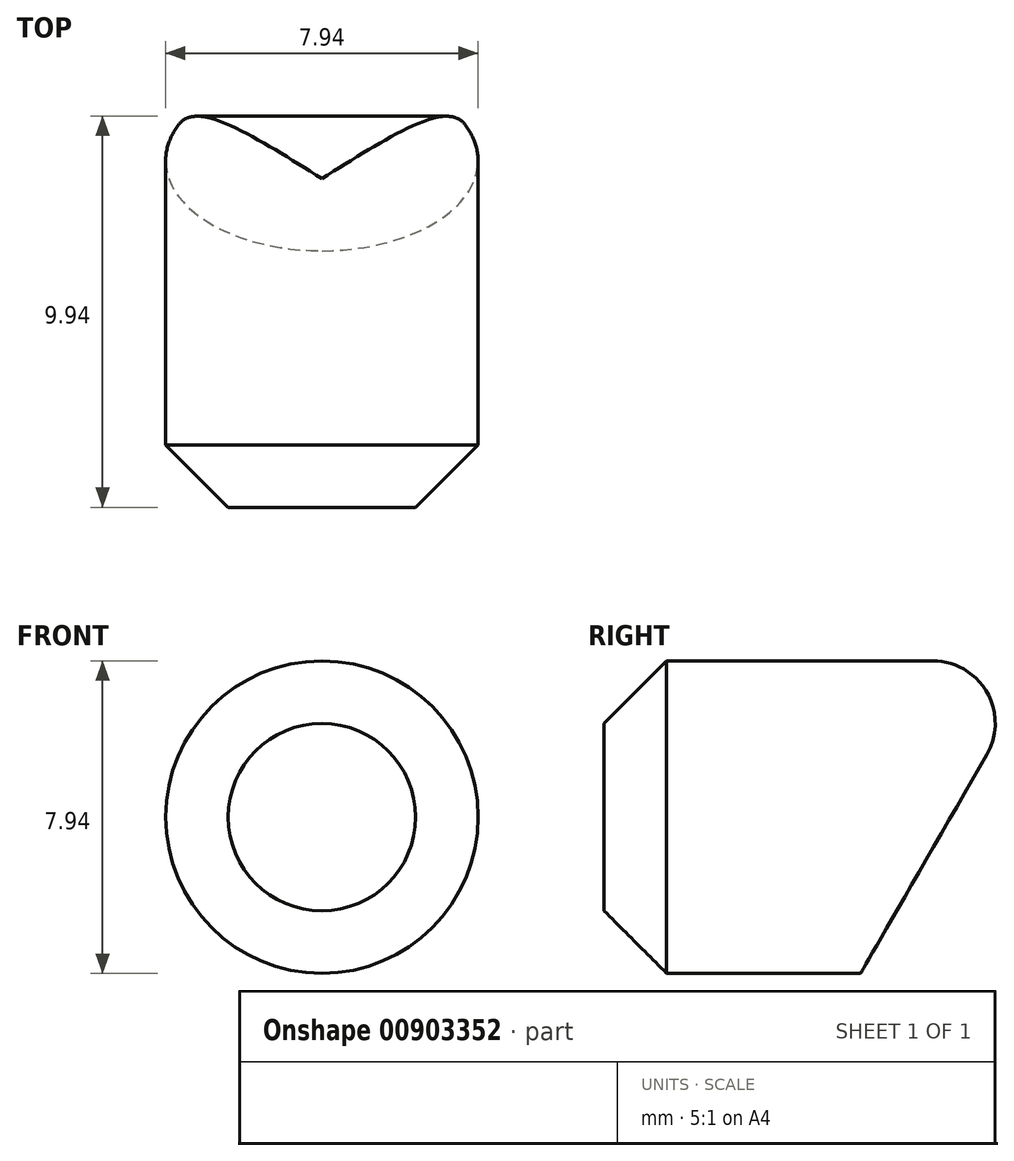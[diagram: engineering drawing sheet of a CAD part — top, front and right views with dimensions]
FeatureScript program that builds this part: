
annotation { "Feature Type Name" : "Feature", "Feature Type Description" : "" }
export const myFeature = defineFeature(function(context is Context, id is Id, definition is map)
    precondition{}
    {
        {
            var Q0;
            Q0=qCreatedBy(makeId("Front.planeOp"),FACE);
            var sketch = newSketch(context, id + "F0", { "sketchPlane" : qUnion([Q0])});
            skCircle(sketch, "E0", {"center": v(0, 0) * mm, "radius": 3.97 * mm});
            skSolve(sketch);
        }
        {
            var Q0;
            Q0=makeQuery(id+"F0.imprint","IMPRINT",FACE,{"disambiguationData":[TD([[makeQuery(id+"F0.imprint","IMPRINT",EDGE,{"derivedFrom":sQuery(id+"F0.wireOp",EDGE,"E0")}),1.0]])]});
            extrude(context, id + "F1", {"entities" : qUnion([Q0]), "oppositeDirection" : true, "depth" : 11.1 * mm, "offsetDistance" : 25.4 * mm});
        }
        {
            var Q0;
            Q0=qCreatedBy(makeId("Right.planeOp"),FACE);
            var sketch = newSketch(context, id + "F2", { "sketchPlane" : qUnion([Q0])});
            skLineSegment(sketch, "E1", {"start": v(11.1, 3.97) * mm, "end": v(-3.56, -21.43) * mm});
            skLineSegment(sketch, "E2", {"start": v(-3.56, -21.43) * mm, "end": v(11.1, -21.43) * mm});
            skLineSegment(sketch, "E3", {"start": v(11.1, -21.43) * mm, "end": v(11.1, 3.97) * mm});
            skLineSegment(sketch, "E4", {"start": v(0, 3.97) * mm, "end": v(11.1, 3.97) * mm});
            skSolve(sketch);
        }
        {
            var Q0;
            Q0=makeQuery(id+"F2.imprint","IMPRINT",FACE,{"disambiguationData":[TD([[makeQuery(id+"F2.imprint","IMPRINT",EDGE,{"derivedFrom":sQuery(id+"F2.wireOp",EDGE,"E1")}),1.0]])]});
            extrude(context, id + "F3", {"entities" : qUnion([Q0]), "operationType" : NewBodyOperationType.REMOVE, "oppositeDirection" : true, "depth" : 25.4 * mm, "offsetDistance" : 25.4 * mm, "hasSecondDirection" : true, "secondDirectionOppositeDirection" : false, "secondDirectionDepth" : 25.4 * mm});
        }
        {
            var Q0;
            Q0=makeQuery(id+"F1.opExtrude","CAP_EDGE",EDGE,{"disambiguationData":[OSD([sQuery(id+"F0.wireOp",EDGE,"E0")])],"isStart":true});
            chamfer(context, id + "F4", {"entities" : qUnion([Q0]), "chamferType" : ChamferType.OFFSET_ANGLE, "width" : 1.59 * mm, "oppositeDirection" : false, "angle" : 45 * degree, "tangentPropagation" : true});
        }
        {
            var Q0;
            Q0=qCreatedBy(makeId("Right.planeOp"),FACE);
            cPlane(context, id + "F5", {"entities" : qUnion([Q0]), "cplaneType" : CPlaneType.OFFSET, "offset" : 0 * mm, "width" : 152.4 * mm, "height" : 152.4 * mm});
        }
        {
            var Q0;
            Q0=qCreatedBy(id+"F5.planeOp",FACE);
            var sketch = newSketch(context, id + "F6", { "sketchPlane" : qUnion([Q0])});
            skLineSegment(sketch, "E5", {"start": v(1.59, 3.97) * mm, "end": v(8.35, 3.97) * mm});
            skLineSegment(sketch, "E6.0", {"start": v(9.72, 1.59) * mm, "end": v(6.52, -3.97) * mm});
            skLineSegment(sketch, "E7", {"start": v(0, 2.38) * mm, "end": v(1.59, 3.97) * mm});
            skLineSegment(sketch, "E8.0", {"start": v(0, -2.38) * mm, "end": v(0, 2.38) * mm});
            skLineSegment(sketch, "E9.0", {"start": v(1.59, 3.97) * mm, "end": v(1.59, -3.97) * mm});
            skPoint(sketch, "E10.visualSharp", {"position": v(11.1, 3.97) * mm});
            skArc(sketch, "E10.filletArc", {"start": v(9.72, 1.59) * mm, "mid": v(9.72, 3.17) * mm, "end": v(8.35, 3.97) * mm});
            skLineSegment(sketch, "E11", {"start": v(8.35, 3.97) * mm, "end": v(11.1, 3.97) * mm});
            skLineSegment(sketch, "E12", {"start": v(11.1, 3.97) * mm, "end": v(9.72, 1.59) * mm});
            skSolve(sketch);
        }
        {
            var Q0;
            Q0 = qSketchRegion(id + "F6", true);
            extrude(context, id + "F7", {"entities" : qUnion([Q0]), "operationType" : NewBodyOperationType.REMOVE, "oppositeDirection" : true, "depth" : 25.4 * mm, "offsetDistance" : 25.4 * mm, "hasSecondDirection" : true, "secondDirectionOppositeDirection" : false, "secondDirectionDepth" : 25.4 * mm});
        }
    });
